# Revit family: Eurolan_Вертикальный организатор с крышкой с пластиковыми пальцами серия D9000 для шкафов шириной 750 мм
name_source: partatom
category: Устройства связи
units: mm (PartAtom-declared; Revit-internal decimal feet)

## family parameters
Всегда вертикально = Да
На основе рабочей плоскости = Нет
Общий = Нет
При загрузке вырезать с полостями = Нет
Размер круглого соединителя = Использовать диаметр
Сохранять ориентацию аннотаций = Нет
Тип детали = Нормальный
Точка расчета площади = Нет

## types (2) — shared parameters
ADSK_Единица измерения = шт
ADSK_Завод-изготовитель = Eurolan
ADSK_Количество = 1
ADSK_Материал = RAL 9005
zero-valued in all types: ADSK_Масса

## per-type parameters (varying)
| type | ADSK_Код изделия | ADSK_Наименование | ADSK_Наименование краткое | Выбор_графики |
| Вертикальный организатор с крышкой_42U | 60A-18-42-16-31BL | Вертикальный организатор с крышкой, 42U, с пластиковыми пальцами, серия D9000 (2 шт.), для шкафов шириной 750 мм | Вертикальный организатор с крышкой, 42U, с пластиковыми пальцами | Вертикальный организатор с крышкой 42U с пластиковыми пальцами |
| Вертикальный организатор с крышкой_48U | 60A-18-48-16-31BL | Вертикальный организатор с крышкой, 48U, с пластиковыми пальцами, серия D9000 (2 шт.), для шкафов шириной 750 мм | Вертикальный организатор с крышкой, 48U, с пластиковыми пальцами | Вертикальный организатор с крышкой 48U с пластиковыми пальцами |
